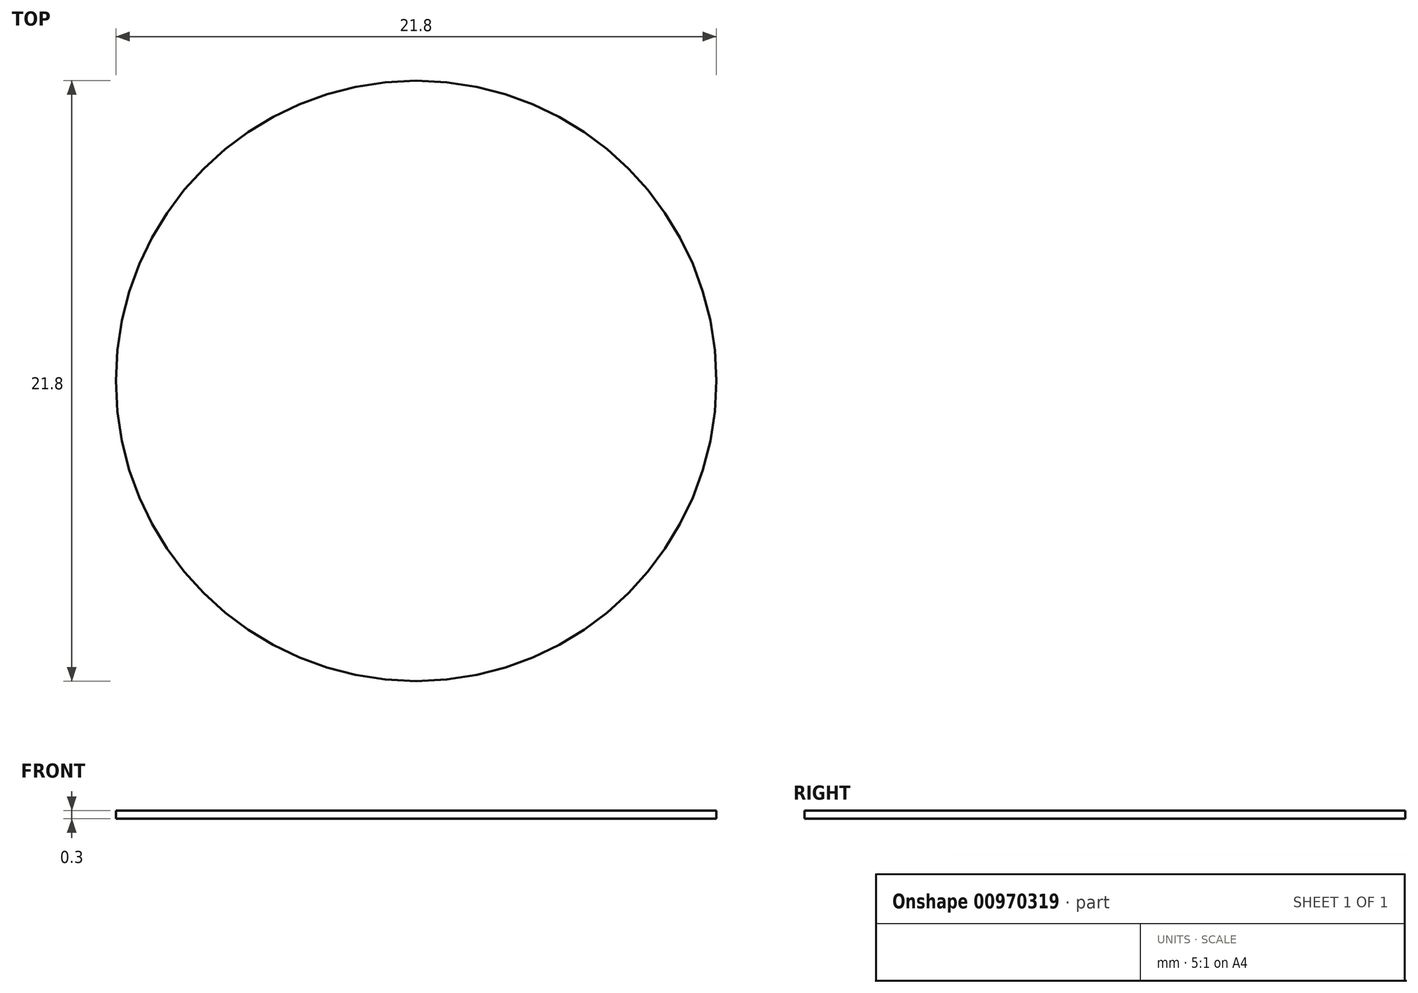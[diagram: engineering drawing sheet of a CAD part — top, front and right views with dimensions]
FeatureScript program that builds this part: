
annotation { "Feature Type Name" : "Feature", "Feature Type Description" : "" }
export const myFeature = defineFeature(function(context is Context, id is Id, definition is map)
    precondition{}
    {
        {
            var Q0;
            Q0=qCreatedBy(makeId("Top.planeOp"),FACE);
            var sketch = newSketch(context, id + "F0", { "sketchPlane" : qUnion([Q0])});
            skCircle(sketch, "E0", {"center": v(0, 0) * mm, "radius": 10.9 * mm});
            skSolve(sketch);
        }
        {
            var Q0;
            Q0 = qSketchRegion(id + "F0", true);
            extrude(context, id + "F1", {"entities" : qUnion([Q0]), "depth" : .3 * mm, "offsetDistance" : 25 * mm});
        }
    });
